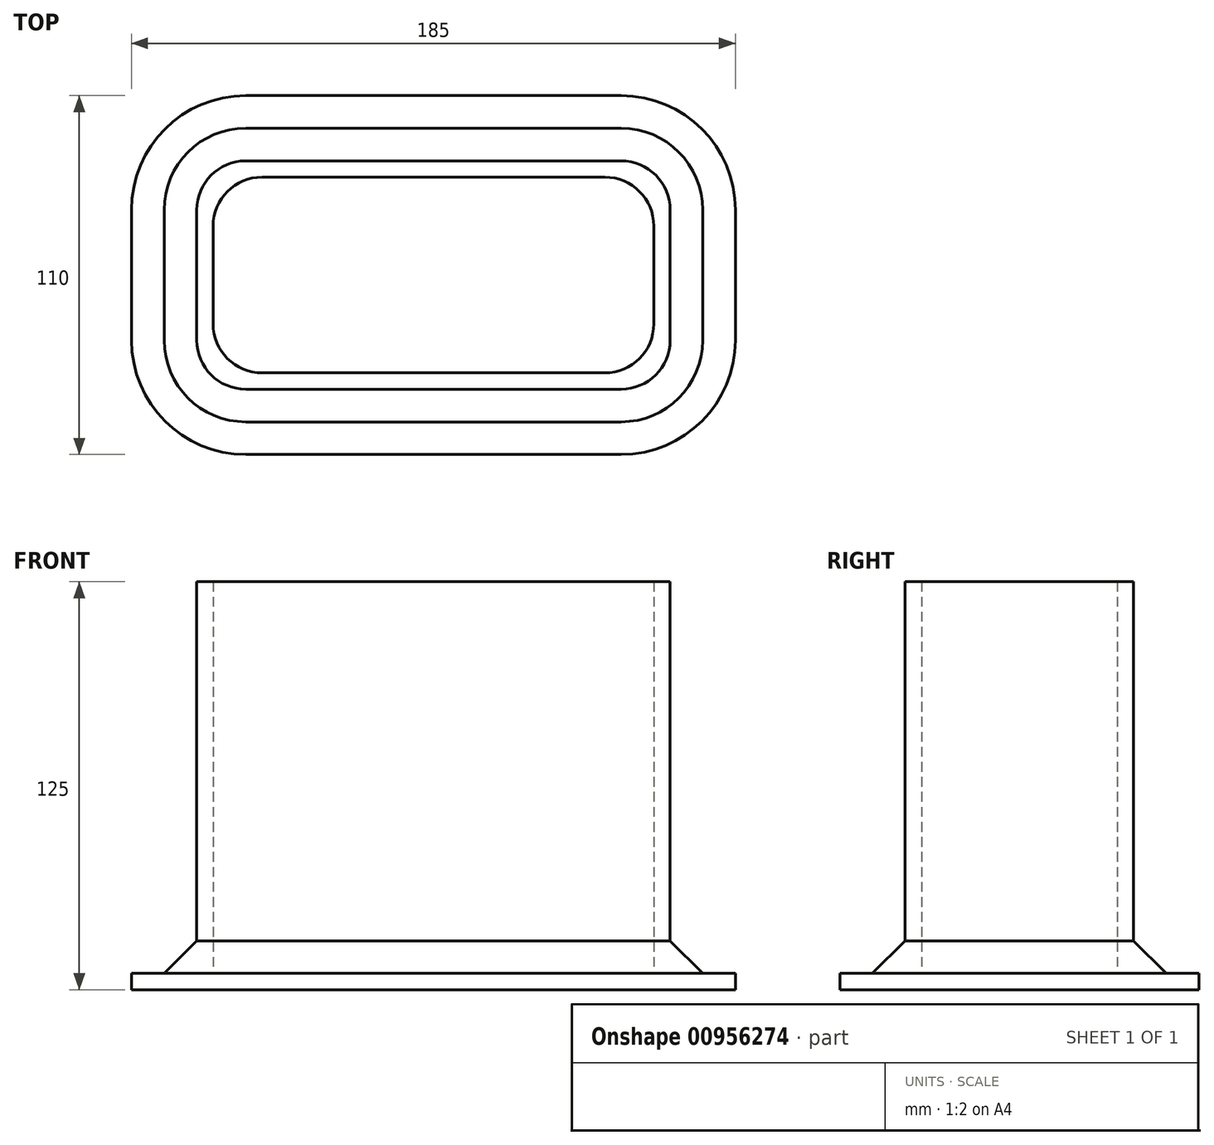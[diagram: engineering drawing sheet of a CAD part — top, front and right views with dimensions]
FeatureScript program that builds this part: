
annotation { "Feature Type Name" : "Feature", "Feature Type Description" : "" }
export const myFeature = defineFeature(function(context is Context, id is Id, definition is map)
    precondition{}
    {
        {
            var Q0;
            Q0=qCreatedBy(makeId("Top.planeOp"),FACE);
            var sketch = newSketch(context, id + "F0", { "sketchPlane" : qUnion([Q0])});
            skLineSegment(sketch, "E0.bottom", {"start": v(67.5, 30) * mm, "end": v(-67.5, 30) * mm});
            skLineSegment(sketch, "E0.top", {"start": v(67.5, -30) * mm, "end": v(-67.5, -30) * mm});
            skLineSegment(sketch, "E0.left", {"start": v(67.5, 30) * mm, "end": v(67.5, -30) * mm});
            skLineSegment(sketch, "E0.right", {"start": v(-67.5, 30) * mm, "end": v(-67.5, -30) * mm});
            skPoint(sketch, "E0.middle", {"position": v(0, 0) * mm});
            skLineSegment(sketch, "E1.0", {"start": v(72.5, 35) * mm, "end": v(-72.5, 35) * mm});
            skLineSegment(sketch, "E1.1", {"start": v(72.5, 35) * mm, "end": v(72.5, -35) * mm});
            skLineSegment(sketch, "E1.2", {"start": v(72.5, -35) * mm, "end": v(-72.5, -35) * mm});
            skLineSegment(sketch, "E1.3", {"start": v(-72.5, 35) * mm, "end": v(-72.5, -35) * mm});
            skSolve(sketch);
        }
        {
            var Q0;
            Q0 = qSketchRegion(id + "F0", true);
            extrude(context, id + "F1", {"entities" : qUnion([Q0]), "depth" : 125 * mm, "offsetDistance" : 25 * mm});
        }
        {
            var Q0;
            Q0=makeQuery(id+"F0.imprint","IMPRINT",FACE,{"disambiguationData":[TD([[makeQuery(id+"F0.imprint","IMPRINT",EDGE,{"derivedFrom":sQuery(id+"F0.wireOp",EDGE,"E0.bottom")}),1.0]])]});
            extrude(context, id + "F2", {"entities" : qUnion([Q0]), "operationType" : NewBodyOperationType.ADD, "depth" : 5 * mm, "offsetDistance" : 25 * mm});
        }
        {
            var Q0;
            Q0=makeQuery(id+"F1.opExtrude","SWEPT_EDGE",EDGE,{"disambiguationData":[OSD([sQuery(id+"F0.wireOp",EDGE,"E1.0"),sQuery(id+"F0.wireOp",EDGE,"E1.3")])]});
            var Q1;
            Q1=makeQuery(id+"F1.opExtrude","SWEPT_EDGE",EDGE,{"disambiguationData":[OSD([sQuery(id+"F0.wireOp",EDGE,"E0.bottom"),sQuery(id+"F0.wireOp",EDGE,"E0.right")])]});
            var Q2;
            Q2=makeQuery(id+"F1.opExtrude","SWEPT_EDGE",EDGE,{"disambiguationData":[OSD([sQuery(id+"F0.wireOp",EDGE,"E0.top"),sQuery(id+"F0.wireOp",EDGE,"E0.right")])]});
            var Q3;
            Q3=makeQuery(id+"F1.opExtrude","SWEPT_EDGE",EDGE,{"disambiguationData":[OSD([sQuery(id+"F0.wireOp",EDGE,"E1.2"),sQuery(id+"F0.wireOp",EDGE,"E1.3")])]});
            var Q4;
            Q4=makeQuery(id+"F1.opExtrude","SWEPT_EDGE",EDGE,{"disambiguationData":[OSD([sQuery(id+"F0.wireOp",EDGE,"E1.1"),sQuery(id+"F0.wireOp",EDGE,"E1.2")])]});
            var Q5;
            Q5=makeQuery(id+"F1.opExtrude","SWEPT_EDGE",EDGE,{"disambiguationData":[OSD([sQuery(id+"F0.wireOp",EDGE,"E0.top"),sQuery(id+"F0.wireOp",EDGE,"E0.left")])]});
            var Q6;
            Q6=makeQuery(id+"F1.opExtrude","SWEPT_EDGE",EDGE,{"disambiguationData":[OSD([sQuery(id+"F0.wireOp",EDGE,"E0.bottom"),sQuery(id+"F0.wireOp",EDGE,"E0.left")])]});
            var Q7;
            Q7=makeQuery(id+"F1.opExtrude","SWEPT_EDGE",EDGE,{"disambiguationData":[OSD([sQuery(id+"F0.wireOp",EDGE,"E1.0"),sQuery(id+"F0.wireOp",EDGE,"E1.1")])]});
            fillet(context, id + "F3", {"entities" : qUnion([Q0, Q1, Q2, Q3, Q4, Q5, Q6, Q7]), "radius" : 15 * mm, "tangentPropagation" : true, "allowEdgeOverflow" : false});
        }
        {
            var Q0;
            {var subQ0=sQuery(id+"F0.wireOp",EDGE,"E0.right");var subQ1=sQuery(id+"F0.wireOp",EDGE,"E0.left");var subQ2=sQuery(id+"F0.wireOp",EDGE,"E0.top");var subQ3=sQuery(id+"F0.wireOp",EDGE,"E0.bottom");Q0=makeQuery(id+"F2.boolean.opBoolean","MERGE",FACE,{"derivedFrom":[makeQuery(id+"F1.opExtrude","CAP_FACE",FACE,{"disambiguationData":[OSD([subQ3,subQ2,subQ1,subQ0,sQuery(id+"F0.wireOp",EDGE,"E1.0"),sQuery(id+"F0.wireOp",EDGE,"E1.1"),sQuery(id+"F0.wireOp",EDGE,"E1.2"),sQuery(id+"F0.wireOp",EDGE,"E1.3")])],"isStart":true}),makeQuery(id+"F2.opExtrude","CAP_FACE",FACE,{"disambiguationData":[OSD([subQ3,subQ2,subQ1,subQ0])],"isStart":true})]});}
            var sketch = newSketch(context, id + "F4", { "sketchPlane" : qUnion([Q0])});
            skArc(sketch, "E2.0", {"start": v(-57.5, 55) * mm, "mid": v(-82.25, 44.75) * mm, "end": v(-92.5, 20) * mm});
            skLineSegment(sketch, "E2.1", {"start": v(57.5, 55) * mm, "end": v(-57.5, 55) * mm});
            skLineSegment(sketch, "E2.2", {"start": v(-92.5, 20) * mm, "end": v(-92.5, -20) * mm});
            skArc(sketch, "E2.3", {"start": v(92.5, 20) * mm, "mid": v(82.25, 44.75) * mm, "end": v(57.5, 55) * mm});
            skArc(sketch, "E2.4", {"start": v(-92.5, -20) * mm, "mid": v(-82.25, -44.75) * mm, "end": v(-57.5, -55) * mm});
            skLineSegment(sketch, "E2.5", {"start": v(-57.5, -55) * mm, "end": v(57.5, -55) * mm});
            skArc(sketch, "E2.6", {"start": v(57.5, -55) * mm, "mid": v(82.25, -44.75) * mm, "end": v(92.5, -20) * mm});
            skLineSegment(sketch, "E2.7", {"start": v(92.5, -20) * mm, "end": v(92.5, 20) * mm});
            skSolve(sketch);
        }
        {
            var Q0;
            Q0 = qSketchRegion(id + "F4", true);
            extrude(context, id + "F5", {"entities" : qUnion([Q0]), "operationType" : NewBodyOperationType.ADD, "oppositeDirection" : true, "depth" : 5 * mm, "offsetDistance" : 25 * mm});
        }
        {
            var Q0;
            Q0=makeQuery(id+"F5.boolean.opBoolean","INTERSECT",EDGE,{"derivedFrom":[makeQuery(id+"F3.opFillet","BLEND_FACE",FACE,{"disambiguationData":[OSD([sQuery(id+"F0.wireOp",EDGE,"E1.0"),sQuery(id+"F0.wireOp",EDGE,"E1.3")])]}),makeQuery(id+"F5.opExtrude","CAP_FACE",FACE,{"disambiguationData":[OSD([sQuery(id+"F4.wireOp",EDGE,"E2.0"),sQuery(id+"F4.wireOp",EDGE,"E2.1"),sQuery(id+"F4.wireOp",EDGE,"E2.2"),sQuery(id+"F4.wireOp",EDGE,"E2.3"),sQuery(id+"F4.wireOp",EDGE,"E2.4"),sQuery(id+"F4.wireOp",EDGE,"E2.5"),sQuery(id+"F4.wireOp",EDGE,"E2.6"),sQuery(id+"F4.wireOp",EDGE,"E2.7")])],"isStart":false})]});
            chamfer(context, id + "F6", {"entities" : qUnion([Q0]), "width" : 10 * mm, "tangentPropagation" : true});
        }
    });
